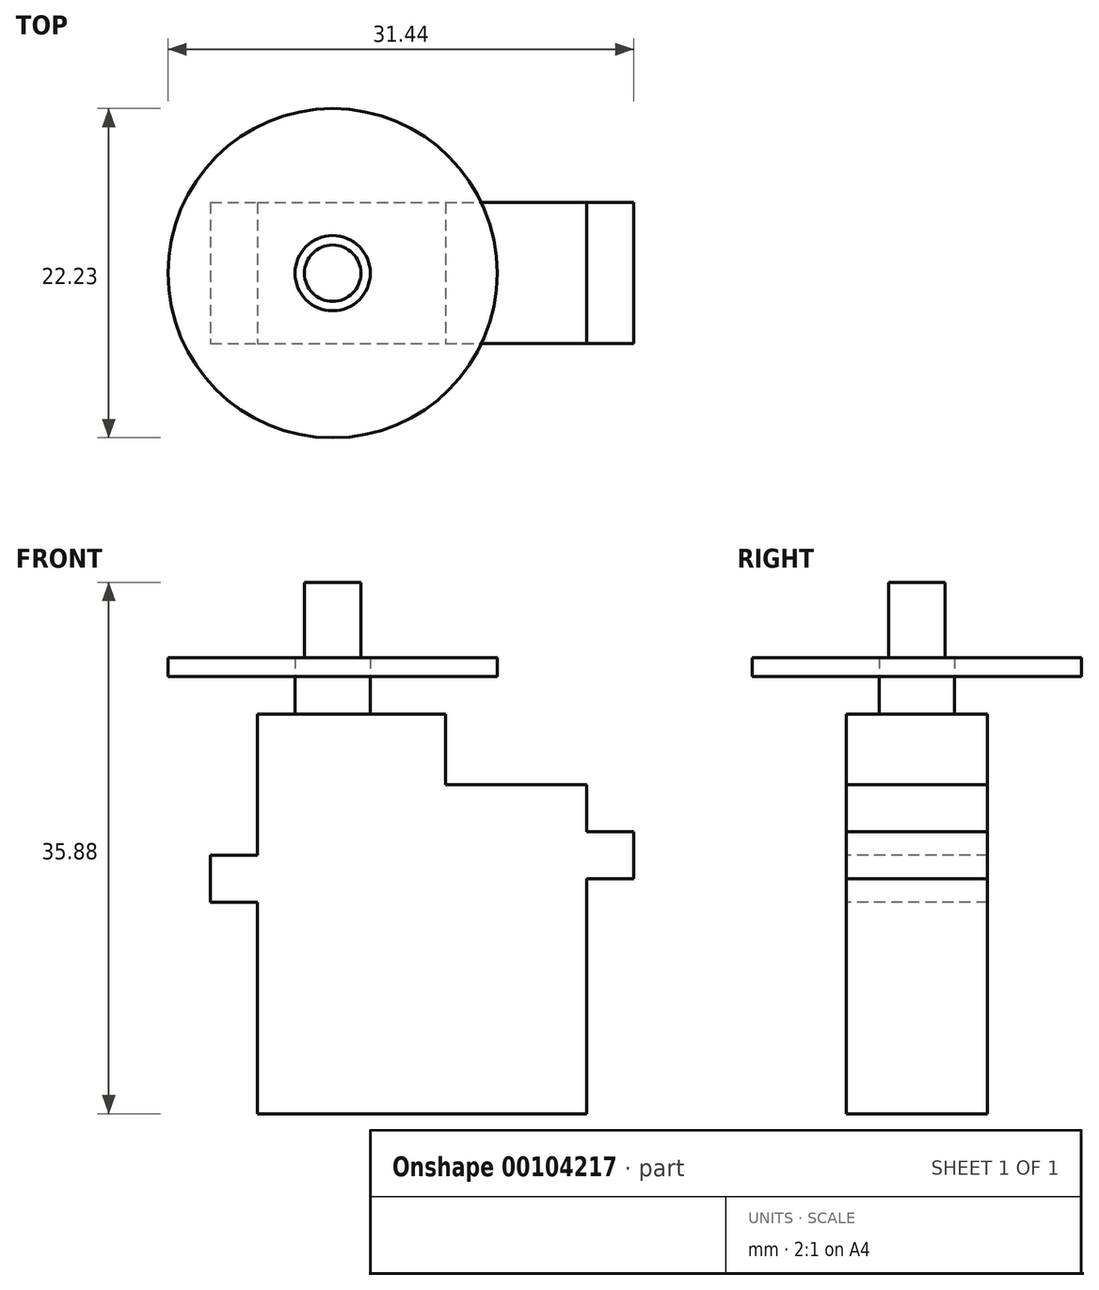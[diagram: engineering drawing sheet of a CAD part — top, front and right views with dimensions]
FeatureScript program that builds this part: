
annotation { "Feature Type Name" : "Feature", "Feature Type Description" : "" }
export const myFeature = defineFeature(function(context is Context, id is Id, definition is map)
    precondition{}
    {
        {
            var Q0;
            Q0=qCreatedBy(makeId("Front.planeOp"),FACE);
            var sketch = newSketch(context, id + "F0", { "sketchPlane" : qUnion([Q0])});
            skLineSegment(sketch, "E0.bottom", {"start": v(-7.34, 2.55) * mm, "end": v(14.89, 2.55) * mm});
            skLineSegment(sketch, "E0.top", {"start": v(-7.34, 24.78) * mm, "end": v(14.89, 24.78) * mm});
            skLineSegment(sketch, "E0.left", {"start": v(-7.34, 2.55) * mm, "end": v(-7.34, 24.78) * mm});
            skLineSegment(sketch, "E0.right", {"start": v(14.89, 2.55) * mm, "end": v(14.89, 24.78) * mm});
            skSolve(sketch);
        }
        {
            var Q0;
            Q0=makeQuery(id+"F0.imprint","IMPRINT",FACE,{"disambiguationData":[TD([[makeQuery(id+"F0.imprint","IMPRINT",EDGE,{"derivedFrom":sQuery(id+"F0.wireOp",EDGE,"E0.bottom")}),1.0]])]});
            extrude(context, id + "F1", {"entities" : qUnion([Q0]), "oppositeDirection" : true, "depth" : 9.52 * mm});
        }
        {
            var Q0;
            Q0=makeQuery(id+"F1.opExtrude","SWEPT_FACE",FACE,{"disambiguationData":[OSD([sQuery(id+"F0.wireOp",EDGE,"E0.top")])]});
            var sketch = newSketch(context, id + "F2", { "sketchPlane" : qUnion([Q0])});
            skLineSegment(sketch, "E1.bottom", {"start": v(-7.34, 9.53) * mm, "end": v(5.36, 9.53) * mm});
            skLineSegment(sketch, "E1.top", {"start": v(-7.34, 0) * mm, "end": v(5.36, 0) * mm});
            skLineSegment(sketch, "E1.left", {"start": v(-7.34, 9.53) * mm, "end": v(-7.34, 0) * mm});
            skLineSegment(sketch, "E1.right", {"start": v(5.36, 9.53) * mm, "end": v(5.36, 0) * mm});
            skSolve(sketch);
        }
        {
            var Q0;
            Q0=makeQuery(id+"F2.imprint","IMPRINT",FACE,{"disambiguationData":[TD([[makeQuery(id+"F2.imprint","IMPRINT",EDGE,{"derivedFrom":sQuery(id+"F2.wireOp",EDGE,"E1.bottom")}),-1.0]])]});
            extrude(context, id + "F3", {"entities" : qUnion([Q0]), "operationType" : NewBodyOperationType.ADD, "depth" : 4.76 * mm});
        }
        {
            var Q0;
            Q0=makeQuery(id+"F1.opExtrude","SWEPT_FACE",FACE,{"disambiguationData":[OSD([sQuery(id+"F0.wireOp",EDGE,"E0.right")])]});
            var sketch = newSketch(context, id + "F4", { "sketchPlane" : qUnion([Q0])});
            skLineSegment(sketch, "E2", {"start": v(0, 24.78) * mm, "end": v(0, 21.6) * mm});
            skLineSegment(sketch, "E3.bottom", {"start": v(0, 21.6) * mm, "end": v(9.53, 21.6) * mm});
            skLineSegment(sketch, "E3.top", {"start": v(0, 18.43) * mm, "end": v(9.53, 18.43) * mm});
            skLineSegment(sketch, "E3.left", {"start": v(0, 21.6) * mm, "end": v(0, 18.43) * mm});
            skLineSegment(sketch, "E3.right", {"start": v(9.53, 21.6) * mm, "end": v(9.53, 18.43) * mm});
            skSolve(sketch);
        }
        {
            var Q0;
            Q0=makeQuery(id+"F4.imprint","IMPRINT",FACE,{"disambiguationData":[TD([[makeQuery(id+"F4.imprint","IMPRINT",EDGE,{"derivedFrom":sQuery(id+"F4.wireOp",EDGE,"E3.bottom")}),-1.0]])]});
            extrude(context, id + "F5", {"entities" : qUnion([Q0]), "operationType" : NewBodyOperationType.ADD, "depth" : 3.17 * mm});
        }
        {
            var Q0;
            Q0=makeQuery(id+"F3.boolean.opBoolean","MERGE",FACE,{"derivedFrom":[makeQuery(id+"F1.opExtrude","SWEPT_FACE",FACE,{"disambiguationData":[OSD([sQuery(id+"F0.wireOp",EDGE,"E0.left")])]}),makeQuery(id+"F3.opExtrude","SWEPT_FACE",FACE,{"disambiguationData":[OSD([sQuery(id+"F2.wireOp",EDGE,"E1.left")])]})]});
            var sketch = newSketch(context, id + "F6", { "sketchPlane" : qUnion([Q0])});
            skLineSegment(sketch, "E4.bottom", {"start": v(-9.52, 20.01) * mm, "end": v(0, 20.01) * mm});
            skLineSegment(sketch, "E4.top", {"start": v(-9.52, 16.84) * mm, "end": v(0, 16.84) * mm});
            skLineSegment(sketch, "E4.left", {"start": v(-9.52, 20.01) * mm, "end": v(-9.52, 16.84) * mm});
            skLineSegment(sketch, "E4.right", {"start": v(0, 20.01) * mm, "end": v(0, 16.84) * mm});
            skLineSegment(sketch, "E5", {"start": v(-9.52, 20.01) * mm, "end": v(-9.53, 29.54) * mm});
            skSolve(sketch);
        }
        {
            var Q0;
            Q0=makeQuery(id+"F6.imprint","IMPRINT",FACE,{"disambiguationData":[TD([[makeQuery(id+"F6.imprint","IMPRINT",EDGE,{"derivedFrom":sQuery(id+"F6.wireOp",EDGE,"E4.bottom")}),-1.0]])]});
            extrude(context, id + "F7", {"entities" : qUnion([Q0]), "operationType" : NewBodyOperationType.ADD, "depth" : 3.17 * mm});
        }
        {
            var Q0;
            Q0=makeQuery(id+"F3.opExtrude","CAP_FACE",FACE,{"disambiguationData":[OSD([sQuery(id+"F2.wireOp",EDGE,"E1.bottom"),sQuery(id+"F2.wireOp",EDGE,"E1.top"),sQuery(id+"F2.wireOp",EDGE,"E1.left"),sQuery(id+"F2.wireOp",EDGE,"E1.right")])],"isStart":false});
            var sketch = newSketch(context, id + "F8", { "sketchPlane" : qUnion([Q0])});
            skLineSegment(sketch, "E6", {"start": v(-7.34, 4.76) * mm, "end": v(-5.75, 4.76) * mm});
            skLineSegment(sketch, "E7", {"start": v(-5.75, 4.76) * mm, "end": v(-2.27, 4.76) * mm});
            skCircle(sketch, "E8", {"center": v(-2.27, 4.76) * mm, "radius": 2.54 * mm});
            skSolve(sketch);
        }
        {
            var Q0;
            Q0=makeQuery(id+"F8.imprint","IMPRINT",FACE,{"disambiguationData":[TD([[makeQuery(id+"F8.imprint","IMPRINT",EDGE,{"derivedFrom":sQuery(id+"F8.wireOp",EDGE,"E8")}),1.0]])]});
            extrude(context, id + "F9", {"entities" : qUnion([Q0]), "operationType" : NewBodyOperationType.ADD, "depth" : 2.54 * mm});
        }
        {
            var Q0;
            Q0=makeQuery(id+"F9.opExtrude","CAP_FACE",FACE,{"disambiguationData":[OSD([sQuery(id+"F8.wireOp",EDGE,"E8")])],"isStart":false});
            var sketch = newSketch(context, id + "F10", { "sketchPlane" : qUnion([Q0])});
            skCircle(sketch, "E9", {"center": v(-2.27, 4.76) * mm, "radius": 11.11 * mm});
            skSolve(sketch);
        }
        {
            var Q0;
            Q0=makeQuery(id+"F10.imprint","IMPRINT",FACE,{"disambiguationData":[TD([[makeQuery(id+"F10.imprint","IMPRINT",EDGE,{"derivedFrom":sQuery(id+"F10.wireOp",EDGE,"E9")}),1.0]])]});
            extrude(context, id + "F11", {"entities" : qUnion([Q0]), "depth" : 1.27 * mm});
        }
        {
            var Q0;
            Q0=makeQuery(id+"F9.opExtrude","CAP_FACE",FACE,{"disambiguationData":[OSD([sQuery(id+"F8.wireOp",EDGE,"E8")])],"isStart":false});
            extrude(context, id + "F12", {"entities" : qUnion([Q0]), "depth" : 1.27 * mm});
        }
        {
            var Q0;
            Q0=makeQuery(id+"F11.opExtrude","CAP_FACE",FACE,{"disambiguationData":[OSD([sQuery(id+"F8.wireOp",EDGE,"E8"),sQuery(id+"F10.wireOp",EDGE,"E9")])],"isStart":false});
            var sketch = newSketch(context, id + "F13", { "sketchPlane" : qUnion([Q0])});
            skCircle(sketch, "E10", {"center": v(-2.27, 4.76) * mm, "radius": 1.9 * mm});
            skSolve(sketch);
        }
        {
            var Q0;
            Q0=makeQuery(id+"F13.imprint","IMPRINT",FACE,{"disambiguationData":[TD([[makeQuery(id+"F13.imprint","IMPRINT",EDGE,{"derivedFrom":sQuery(id+"F13.wireOp",EDGE,"E10")}),1.0]])]});
            extrude(context, id + "F14", {"entities" : qUnion([Q0]), "operationType" : NewBodyOperationType.ADD, "depth" : 5.08 * mm});
        }
    });
